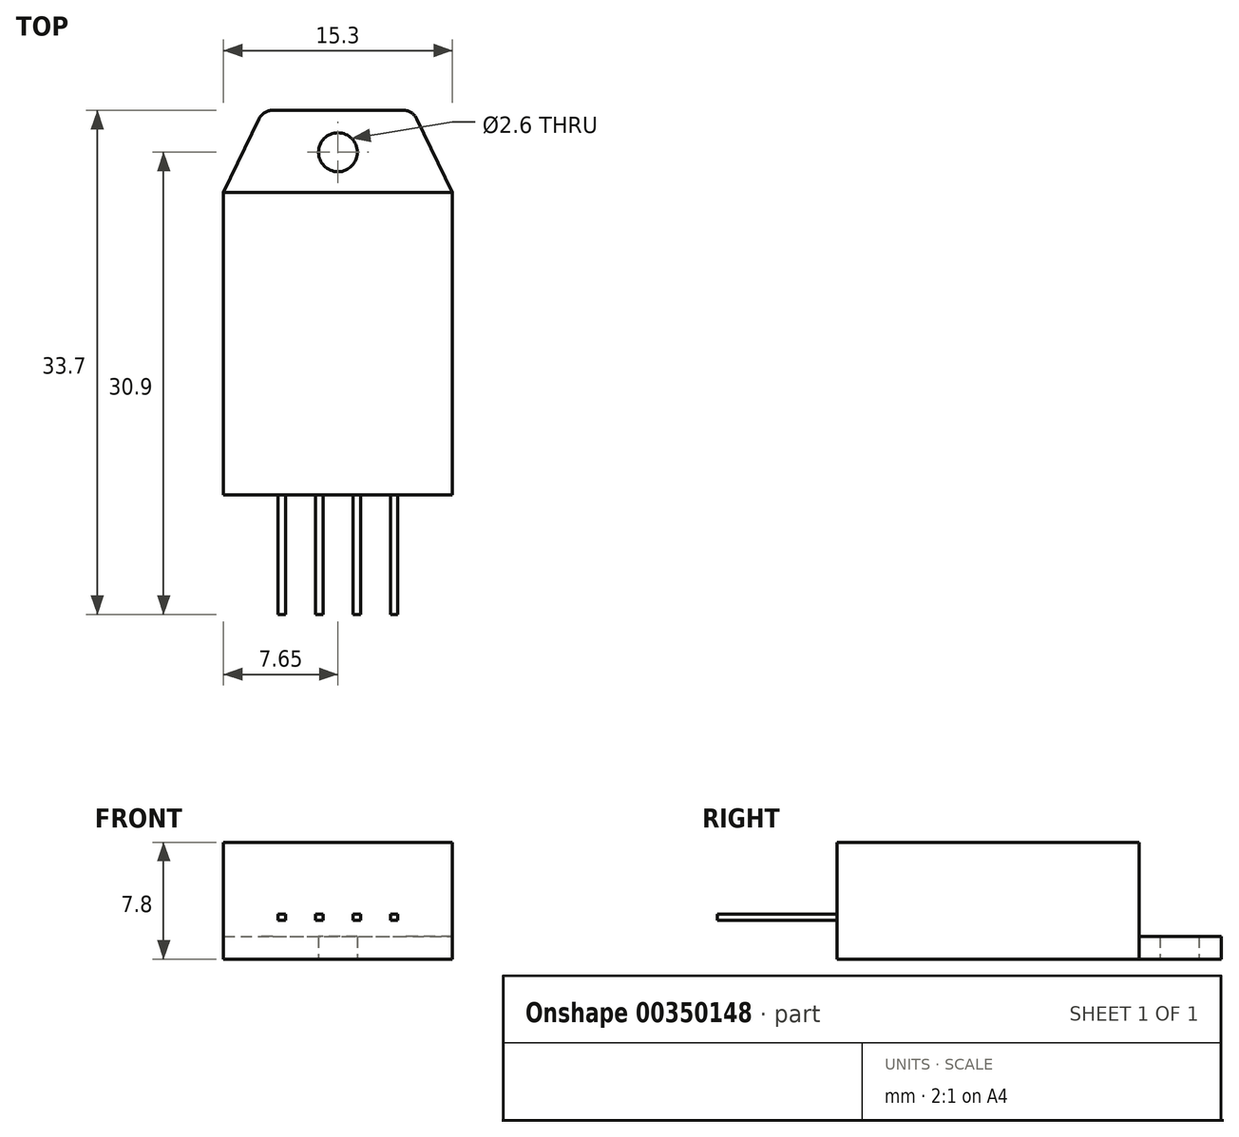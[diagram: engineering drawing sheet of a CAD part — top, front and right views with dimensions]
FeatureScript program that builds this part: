
annotation { "Feature Type Name" : "Feature", "Feature Type Description" : "" }
export const myFeature = defineFeature(function(context is Context, id is Id, definition is map)
    precondition{}
    {
        {
            var Q0;
            Q0=qCreatedBy(makeId("Top.planeOp"),FACE);
            var sketch = newSketch(context, id + "F0", { "sketchPlane" : qUnion([Q0])});
            skCircle(sketch, "E0", {"center": v(0, 0) * mm, "radius": 1.3 * mm});
            skLineSegment(sketch, "E1", {"start": v(-7.65, -22.9) * mm, "end": v(-7.65, -2.7) * mm});
            skLineSegment(sketch, "E2", {"start": v(-7.65, -2.7) * mm, "end": v(-5.27, 2.23) * mm});
            skLineSegment(sketch, "E3.MirrorCS", {"start": v(7.65, -2.7) * mm, "end": v(5.27, 2.23) * mm});
            skLineSegment(sketch, "E4.MirrorCS", {"start": v(7.65, -22.9) * mm, "end": v(7.65, -2.7) * mm});
            skLineSegment(sketch, "E5", {"start": v(-4.37, 2.8) * mm, "end": v(4.37, 2.8) * mm});
            skLineSegment(sketch, "E6", {"start": v(-7.65, -22.9) * mm, "end": v(7.65, -22.9) * mm});
            skLineSegment(sketch, "E7", {"start": v(-7.65, -2.7) * mm, "end": v(7.65, -2.7) * mm});
            skPoint(sketch, "E8.visualSharp", {"position": v(-5, 2.8) * mm});
            skArc(sketch, "E8.filletArc", {"start": v(-4.37, 2.8) * mm, "mid": v(-4.9, 2.65) * mm, "end": v(-5.27, 2.23) * mm});
            skPoint(sketch, "E9.visualSharp", {"position": v(5, 2.8) * mm});
            skArc(sketch, "E9.filletArc", {"start": v(5.27, 2.23) * mm, "mid": v(4.9, 2.65) * mm, "end": v(4.37, 2.8) * mm});
            skSolve(sketch);
        }
        {
            var Q0;
            Q0=makeQuery(id+"F0.imprint","IMPRINT",FACE,{"disambiguationData":[TD([[makeQuery(id+"F0.imprint","IMPRINT",EDGE,{"derivedFrom":sQuery(id+"F0.wireOp",EDGE,"E0")}),-1.0]])]});
            extrude(context, id + "F1", {"entities" : qUnion([Q0]), "depth" : 1.5 * mm});
        }
        {
            var Q0;
            Q0=makeQuery(id+"F0.imprint","IMPRINT",FACE,{"disambiguationData":[TD([[makeQuery(id+"F0.imprint","IMPRINT",EDGE,{"derivedFrom":sQuery(id+"F0.wireOp",EDGE,"E1")}),-1.0]])]});
            extrude(context, id + "F2", {"entities" : qUnion([Q0]), "operationType" : NewBodyOperationType.ADD, "depth" : 7.8 * mm});
        }
        {
            var Q0;
            Q0=makeQuery(id+"F2.opExtrude","SWEPT_FACE",FACE,{"disambiguationData":[OSD([sQuery(id+"F0.wireOp",EDGE,"E6")])]});
            var sketch = newSketch(context, id + "F3", { "sketchPlane" : qUnion([Q0])});
            skLineSegment(sketch, "E10.bottom", {"start": v(-4, 3) * mm, "end": v(-3.5, 3) * mm});
            skLineSegment(sketch, "E10.top", {"start": v(-4, 2.6) * mm, "end": v(-3.5, 2.6) * mm});
            skLineSegment(sketch, "E10.left", {"start": v(-4, 3) * mm, "end": v(-4, 2.6) * mm});
            skLineSegment(sketch, "E10.right", {"start": v(-3.5, 3) * mm, "end": v(-3.5, 2.6) * mm});
            skLineSegment(sketch, "E11.1.0.0", {"start": v(-1, 3) * mm, "end": v(-1, 2.6) * mm});
            skLineSegment(sketch, "E11.1.0.1", {"start": v(-1.5, 3) * mm, "end": v(-1.5, 2.6) * mm});
            skLineSegment(sketch, "E11.1.0.2", {"start": v(-1.5, 2.6) * mm, "end": v(-1, 2.6) * mm});
            skLineSegment(sketch, "E11.1.0.3", {"start": v(-1.5, 3) * mm, "end": v(-1, 3) * mm});
            skLineSegment(sketch, "E11.2.0.0", {"start": v(1.5, 3) * mm, "end": v(1.5, 2.6) * mm});
            skLineSegment(sketch, "E11.2.0.1", {"start": v(1, 3) * mm, "end": v(1, 2.6) * mm});
            skLineSegment(sketch, "E11.2.0.2", {"start": v(1, 2.6) * mm, "end": v(1.5, 2.6) * mm});
            skLineSegment(sketch, "E11.2.0.3", {"start": v(1, 3) * mm, "end": v(1.5, 3) * mm});
            skLineSegment(sketch, "E11.3.0.0", {"start": v(4, 3) * mm, "end": v(4, 2.6) * mm});
            skLineSegment(sketch, "E11.3.0.1", {"start": v(3.5, 3) * mm, "end": v(3.5, 2.6) * mm});
            skLineSegment(sketch, "E11.3.0.2", {"start": v(3.5, 2.6) * mm, "end": v(4, 2.6) * mm});
            skLineSegment(sketch, "E11.3.0.3", {"start": v(3.5, 3) * mm, "end": v(4, 3) * mm});
            skLineSegment(sketch, "E11.direction1", {"start": v(-4, 2.6) * mm, "end": v(-1.5, 2.6) * mm, "construction": true});
            skSolve(sketch);
        }
        {
            var Q0;
            Q0=qSketchRegion(id+"F3",true);
            extrude(context, id + "F4", {"entities" : qUnion([Q0]), "operationType" : NewBodyOperationType.ADD, "depth" : 8 * mm});
        }
    });
